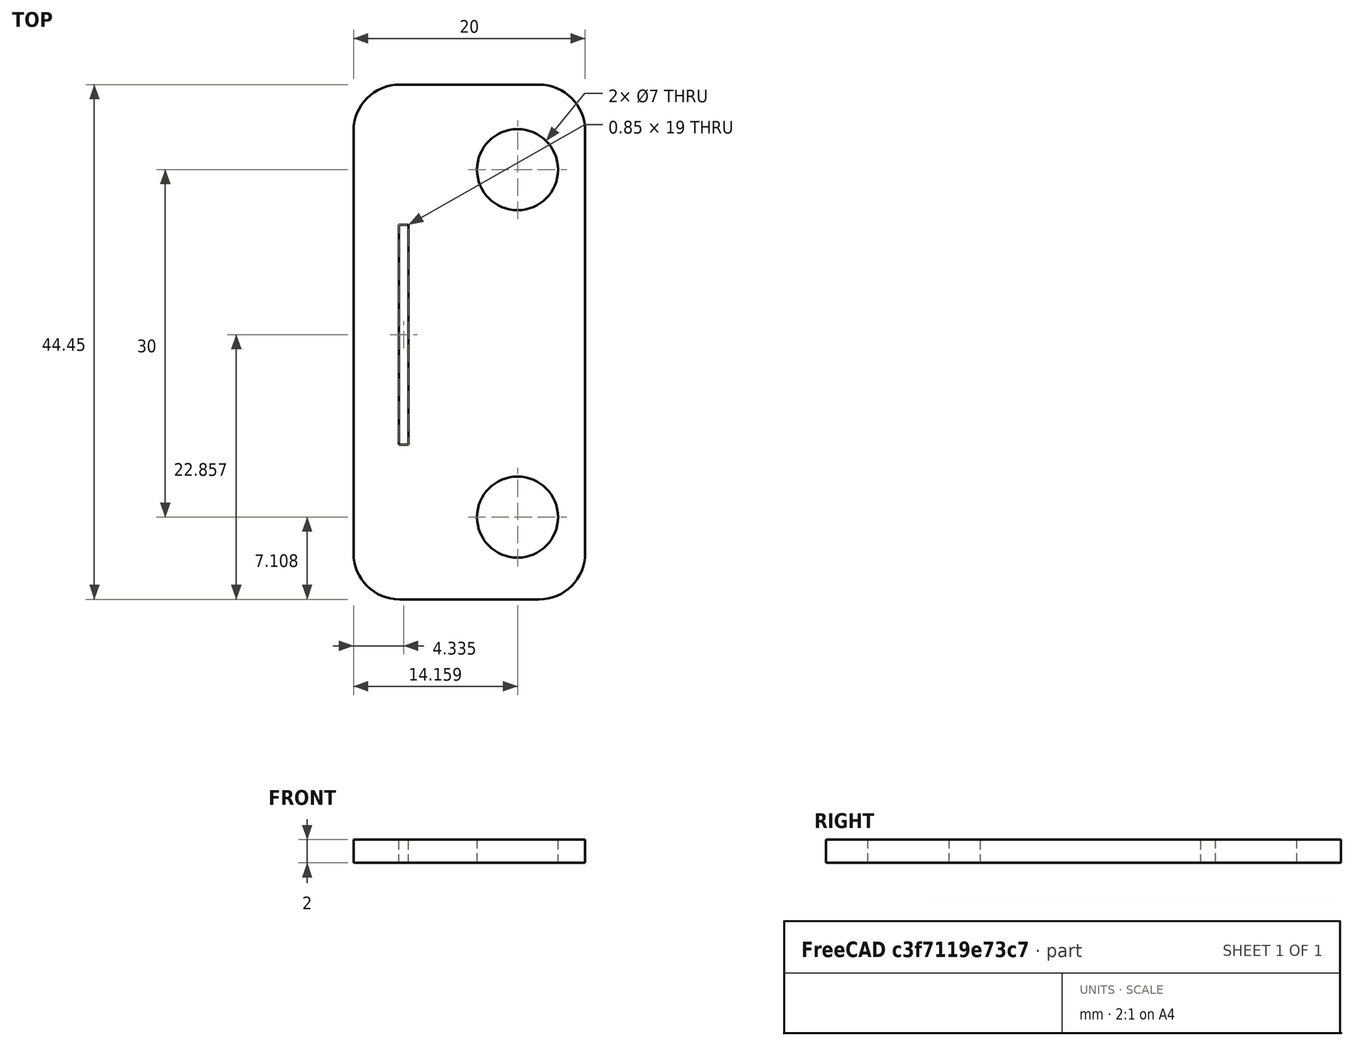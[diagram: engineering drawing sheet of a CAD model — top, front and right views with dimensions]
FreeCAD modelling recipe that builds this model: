
FCSTD DOCUMENT  (FreeCAD 1.0R39319 (Git))
Label: rp2040
License: All rights reserved
LicenseURL: https://en.wikipedia.org/wiki/All_rights_reserved
objects: Sketcher::SketchObject×1, PartDesign::Pad×1, PartDesign::Body×1
note: 6 computed .brp shape members not serialized (recipe doc carries the construction recipe); baked Part::Feature solids carry a one-line shape summary decoded from their .brp

FEATURE [Sketcher::SketchObject] Sketch001
  ArcFitTolerance = 1e-06
  AttachmentSupport = -> [XY_Plane001]
  FullyConstrained = false
  MakeInternals = false
  MapMode = 5
  sketch-geometry (16):
    g0: LineSegment StartX=0 StartY=-4 StartZ=0 EndX=0 EndY=-40.45 EndZ=0
    g1: LineSegment StartX=4 StartY=-44.45 StartZ=0 EndX=16 EndY=-44.45 EndZ=0
    g2: LineSegment StartX=20 StartY=-40.45 StartZ=0 EndX=20 EndY=-4 EndZ=0
    g3: LineSegment StartX=16 StartY=0 StartZ=0 EndX=4 EndY=0 EndZ=0
    g4: ArcOfCircle CenterX=4 CenterY=-4 CenterZ=0 NormalX=0 NormalY=0 NormalZ=1 AngleXU=0 Radius=4 StartAngle=1.5708 EndAngle=3.14159
    g5: ArcOfCircle CenterX=4 CenterY=-40.45 CenterZ=0 NormalX=0 NormalY=0 NormalZ=1 AngleXU=0 Radius=4 StartAngle=3.14159 EndAngle=4.71239
    g6: ArcOfCircle CenterX=16 CenterY=-40.45 CenterZ=0 NormalX=0 NormalY=0 NormalZ=1 AngleXU=0 Radius=4 StartAngle=4.71239 EndAngle=6.28319
    g7: ArcOfCircle CenterX=16 CenterY=-4 CenterZ=0 NormalX=0 NormalY=0 NormalZ=1 AngleXU=0 Radius=4 StartAngle=0 EndAngle=1.5708
    g8: GeomPoint [constr] X=0 Y=0 Z=0
    g9: GeomPoint [constr] X=20 Y=-44.45 Z=0
    g10: Circle CenterX=14.1591 CenterY=-37.3419 CenterZ=0 NormalX=0 NormalY=0 NormalZ=1 AngleXU=0 Radius=3.5
    g11: Circle CenterX=14.1591 CenterY=-7.34189 CenterZ=0 NormalX=0 NormalY=0 NormalZ=1 AngleXU=0 Radius=3.5
    g12: LineSegment StartX=3.90973 StartY=-12.093 StartZ=0 EndX=3.90973 EndY=-31.093 EndZ=0
    g13: LineSegment StartX=3.90973 StartY=-31.093 StartZ=0 EndX=4.75973 EndY=-31.093 EndZ=0
    g14: LineSegment StartX=4.75973 StartY=-31.093 StartZ=0 EndX=4.75973 EndY=-12.093 EndZ=0
    g15: LineSegment StartX=4.75973 StartY=-12.093 StartZ=0 EndX=3.90973 EndY=-12.093 EndZ=0
  constraints (38):
    c: Tangent(g0,g4) = -1.5708
    c: Tangent(g0,g5) = -1.5708
    c: Tangent(g1,g5) = -1.5708
    c: Tangent(g1,g6) = -1.5708
    c: Tangent(g2,g6) = -1.5708
    c: Tangent(g2,g7) = -1.5708
    c: Tangent(g3,g7) = -1.5708
    c: Tangent(g3,g4) = -1.5708
    c: Vertical(g0)
    c: Vertical(g2)
    c: Horizontal(g1)
    c: Horizontal(g3)
    c: Equal(g4,g5)
    c: Equal(g5,g6)
    c: Equal(g6,g7)
    c: PointOnObject(g8,g0)
    c: PointOnObject(g8,g3)
    c: PointOnObject(g9,g1)
    c: PointOnObject(g9,g2)
    c: Distance(g0,g2) = 20
    c: Distance(g1,g3) = 44.45
    c: Radius(g5) = 4
    c: Horizontal(g-1,g8)
    c: Vertical(g-1,g8)
    c: Diameter(g10) = 7
    c: Diameter(g11) = 7
    c: Vertical(g10,g11)
    c: DistanceY(g10,g11) = 30
    c: Coincident(g12,g13)
    c: Coincident(g13,g14)
    c: Coincident(g14,g15)
    c: Coincident(g15,g12)
    c: Vertical(g12)
    c: Vertical(g14)
    c: Horizontal(g13)
    c: Horizontal(g15)
    c: Distance(g12,g14) = 0.85
    c: Distance(g13,g15) = 19
FEATURE [PartDesign::Pad] Pad
  Direction = (0,0,1)
  Length = 2
  Length2 = 10
  Profile = -> Sketch001
  ReferenceAxis = -> Sketch001 [N_Axis]
  Refine = true
  Suppressed = false
  Type = 0
FEATURE [PartDesign::Body] Body001
  AllowCompound = false
  Group = -> [Sketch001,Pad]
  Origin = -> Origin001
  Tip = -> Pad
